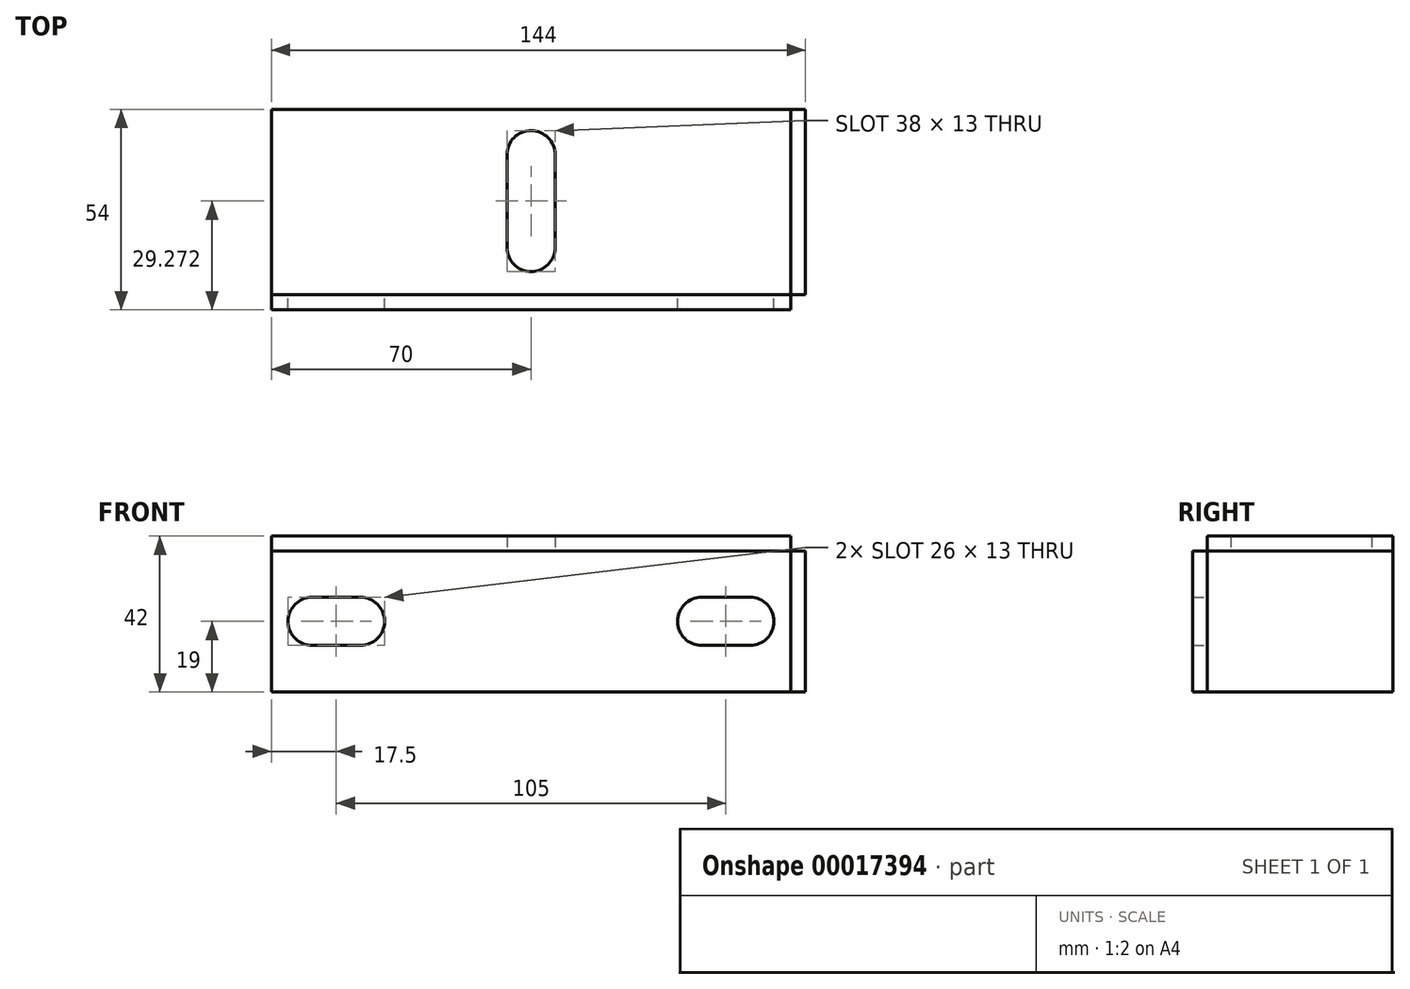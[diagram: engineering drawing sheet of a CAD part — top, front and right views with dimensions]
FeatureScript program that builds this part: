
annotation { "Feature Type Name" : "Feature", "Feature Type Description" : "" }
export const myFeature = defineFeature(function(context is Context, id is Id, definition is map)
    precondition{}
    {
        {
            var Q0;
            Q0=qCreatedBy(makeId("Front.planeOp"),FACE);
            var sketch = newSketch(context, id + "F0", { "sketchPlane" : qUnion([Q0])});
            skLineSegment(sketch, "E0.rect.bottom", {"start": v(70, -19) * mm, "end": v(-70, -19) * mm});
            skLineSegment(sketch, "E0.rect.top", {"start": v(70, 19) * mm, "end": v(-70, 19) * mm});
            skLineSegment(sketch, "E0.rect.left", {"start": v(70, -19) * mm, "end": v(70, 19) * mm});
            skLineSegment(sketch, "E0.rect.right", {"start": v(-70, -19) * mm, "end": v(-70, 19) * mm});
            skPoint(sketch, "E0.rect.middle", {"position": v(0, 0) * mm});
            skLineSegment(sketch, "E1", {"start": v(0, 19) * mm, "end": v(0, -19) * mm, "construction": true});
            skLineSegment(sketch, "E2", {"start": v(-52.5, 6.5) * mm, "end": v(-52.5, 6.5) * mm});
            skArc(sketch, "E3", {"start": v(-59, 6.5) * mm, "mid": v(-65.5, 0) * mm, "end": v(-59, -6.5) * mm});
            skArc(sketch, "E4", {"start": v(-46, -6.5) * mm, "mid": v(-39.5, 0) * mm, "end": v(-46, 6.5) * mm});
            skLineSegment(sketch, "E5", {"start": v(-59, -6.5) * mm, "end": v(-46, -6.5) * mm});
            skLineSegment(sketch, "E6", {"start": v(-46, 6.5) * mm, "end": v(-59, 6.5) * mm});
            skLineSegment(sketch, "E7.trimOffspring", {"start": v(-52.5, -6.5) * mm, "end": v(-52.5, -6.5) * mm});
            skArc(sketch, "E8.MirrorCS", {"start": v(46, -6.5) * mm, "mid": v(39.5, 0) * mm, "end": v(46, 6.5) * mm});
            skLineSegment(sketch, "E9.MirrorCS", {"start": v(59, -6.5) * mm, "end": v(46, -6.5) * mm});
            skArc(sketch, "E10.MirrorCS", {"start": v(59, 6.5) * mm, "mid": v(65.5, 0) * mm, "end": v(59, -6.5) * mm});
            skLineSegment(sketch, "E11.MirrorCS", {"start": v(46, 6.5) * mm, "end": v(59, 6.5) * mm});
            skSolve(sketch);
        }
        {
            var Q0;
            Q0 = qSketchRegion(id + "F0", true);
            extrude(context, id + "F1", {"entities" : qUnion([Q0]), "depth" : 4 * mm});
        }
        {
            var Q0;
            Q0=makeQuery(id+"F1.opExtrude","SWEPT_FACE",FACE,{"disambiguationData":[OSD([sQuery(id+"F0.wireOp",EDGE,"E0.rect.top")])]});
            var sketch = newSketch(context, id + "F2", { "sketchPlane" : qUnion([Q0])});
            skLineSegment(sketch, "E12.bottom", {"start": v(-70, 0) * mm, "end": v(70, 0) * mm});
            skLineSegment(sketch, "E12.top", {"start": v(-70, 50) * mm, "end": v(70, 50) * mm});
            skLineSegment(sketch, "E12.left", {"start": v(-70, 0) * mm, "end": v(-70, 50) * mm});
            skLineSegment(sketch, "E12.right", {"start": v(70, 0) * mm, "end": v(70, 50) * mm});
            skLineSegment(sketch, "E13", {"start": v(0, 50) * mm, "end": v(0, 31.5) * mm, "construction": true});
            skLineSegment(sketch, "E14.trimOffspring", {"start": v(0, 25.54) * mm, "end": v(0, 0) * mm, "construction": true});
            skPoint(sketch, "E15.center.orphan", {"position": v(0, 31.5) * mm});
            skPoint(sketch, "E16.start.orphan", {"position": v(6.5, 12.77) * mm});
            skPoint(sketch, "E17.trimOffspring.end.orphan", {"position": v(6.5, 18.44) * mm});
            skPoint(sketch, "E18.center.orphan", {"position": v(0.01, 18.5) * mm});
            skPoint(sketch, "E19.center.orphan", {"position": v(0.01, 25) * mm});
            skArc(sketch, "E20", {"start": v(-6.5, 12.77) * mm, "mid": v(0, 6.27) * mm, "end": v(6.5, 12.77) * mm});
            skLineSegment(sketch, "E21", {"start": v(-6.5, 12.77) * mm, "end": v(-6.5, 37.77) * mm});
            skLineSegment(sketch, "E22", {"start": v(6.5, 37.77) * mm, "end": v(6.5, 12.77) * mm});
            skPoint(sketch, "E23", {"position": v(0, 37.77) * mm});
            skArc(sketch, "E24", {"start": v(6.5, 37.77) * mm, "mid": v(0, 44.27) * mm, "end": v(-6.5, 37.77) * mm});
            skPoint(sketch, "E25.center.orphan", {"position": v(0, 42.21) * mm});
            skPoint(sketch, "E25.end.orphan", {"position": v(6.5, 42.6) * mm});
            skPoint(sketch, "E26.orphan", {"position": v(-6.5, 41.83) * mm});
            skSolve(sketch);
        }
        {
            var Q0;
            Q0 = qSketchRegion(id + "F2", true);
            extrude(context, id + "F3", {"entities" : qUnion([Q0]), "depth" : 4 * mm});
        }
        {
            var Q0;
            Q0=makeQuery(id+"F3.opExtrude","SWEPT_FACE",FACE,{"disambiguationData":[OSD([sQuery(id+"F2.wireOp",EDGE,"E12.right")])]});
            var sketch = newSketch(context, id + "F4", { "sketchPlane" : qUnion([Q0])});
            skLineSegment(sketch, "E27.bottom", {"start": v(50, 19) * mm, "end": v(0, 19) * mm});
            skLineSegment(sketch, "E27.top", {"start": v(50, -19) * mm, "end": v(0, -19) * mm});
            skLineSegment(sketch, "E27.left", {"start": v(50, 19) * mm, "end": v(50, -19) * mm});
            skLineSegment(sketch, "E27.right", {"start": v(0, 19) * mm, "end": v(0, -19) * mm});
            skSolve(sketch);
        }
        {
            var Q0;
            Q0 = qSketchRegion(id + "F4", true);
            extrude(context, id + "F5", {"entities" : qUnion([Q0]), "depth" : 4 * mm});
        }
    });
